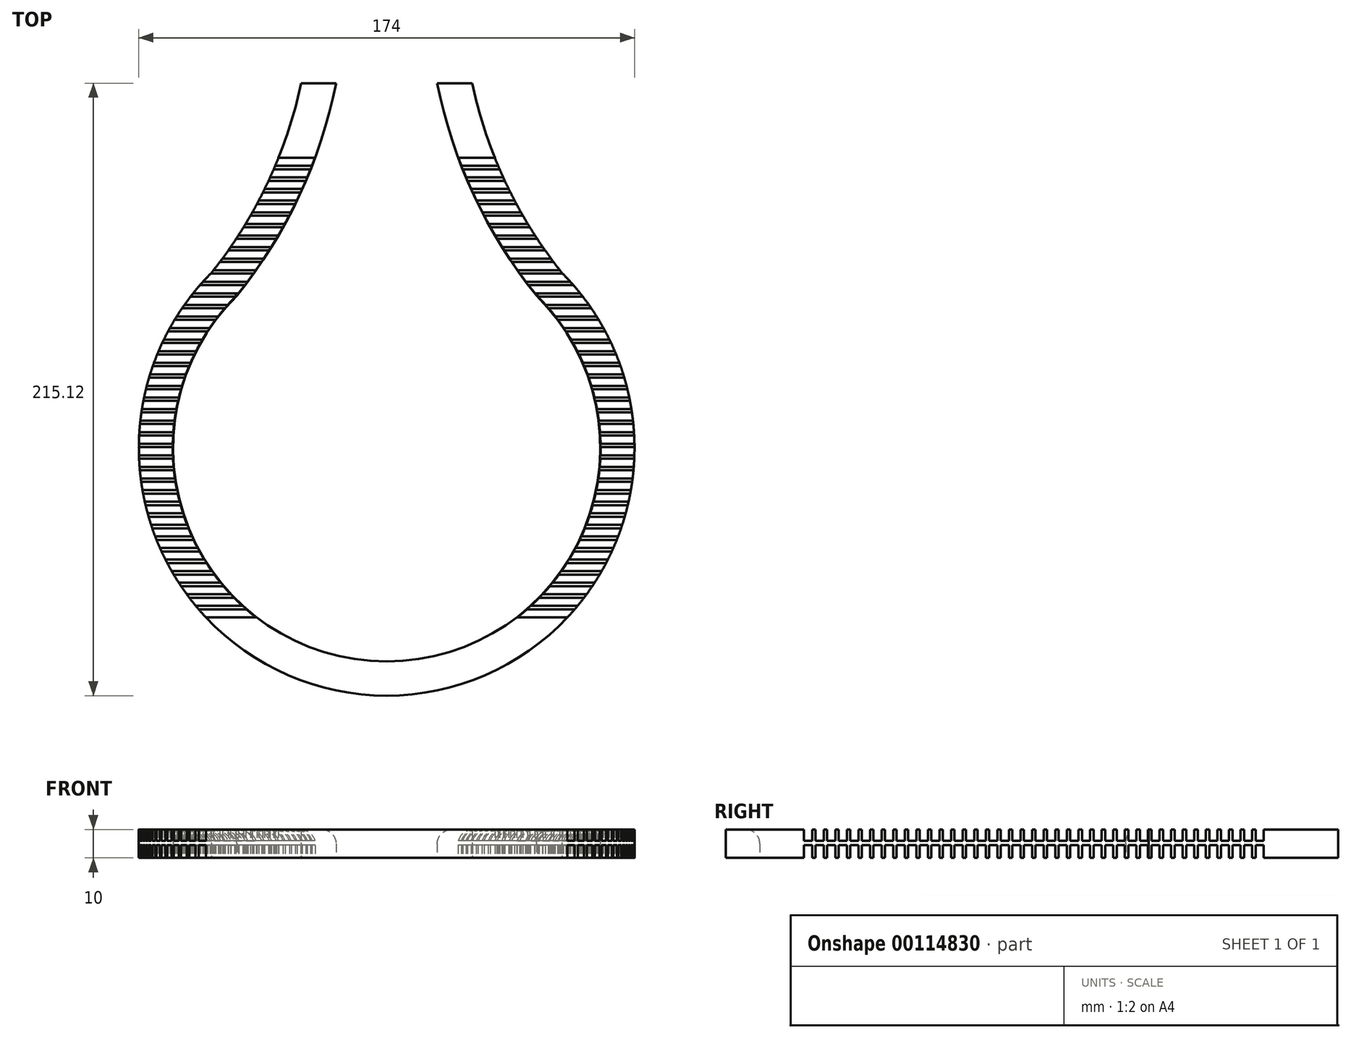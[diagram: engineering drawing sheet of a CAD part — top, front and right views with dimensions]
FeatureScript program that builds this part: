
annotation { "Feature Type Name" : "Feature", "Feature Type Description" : "" }
export const myFeature = defineFeature(function(context is Context, id is Id, definition is map)
    precondition{}
    {
        {
            var Q0;
            Q0=qCreatedBy(makeId("Top.planeOp"),FACE);
            var sketch = newSketch(context, id + "F0", { "sketchPlane" : qUnion([Q0])});
            skArc(sketch, "E0", {"start": v(-52.59, 53.48) * mm, "mid": v(0, -75) * mm, "end": v(52.59, 53.48) * mm});
            skArc(sketch, "E1.0", {"start": v(-61.52, 61.52) * mm, "mid": v(0, -87) * mm, "end": v(61.52, 61.52) * mm});
            skLineSegment(sketch, "E2.bottom", {"start": v(-30, 128.12) * mm, "end": v(-17.75, 128.12) * mm});
            skLineSegment(sketch, "E3", {"start": v(0, 0) * mm, "end": v(-86.34, 86.34) * mm, "construction": true});
            skLineSegment(sketch, "E4", {"start": v(0, 0) * mm, "end": v(95.2, 95.2) * mm, "construction": true});
            skArc(sketch, "E5", {"start": v(-61.52, 61.52) * mm, "mid": v(-41.87, 92.98) * mm, "end": v(-30, 128.12) * mm});
            skArc(sketch, "E6", {"start": v(30, 128.12) * mm, "mid": v(41.87, 92.98) * mm, "end": v(61.52, 61.52) * mm});
            skArc(sketch, "E7.0", {"start": v(-60.47, 44.37) * mm, "mid": v(-33.27, 83.27) * mm, "end": v(-17.75, 128.12) * mm});
            skArc(sketch, "E8.0", {"start": v(17.75, 128.12) * mm, "mid": v(33.27, 83.27) * mm, "end": v(60.47, 44.37) * mm});
            skLineSegment(sketch, "E9", {"start": v(17.75, 128.12) * mm, "end": v(30, 128.12) * mm});
            skSolve(sketch);
        }
        {
            var Q0;
            Q0=makeQuery(id+"F0.imprint","IMPRINT",FACE,{"disambiguationData":[TD([[makeQuery(id+"F0.imprint","IMPRINT",EDGE,{"derivedFrom":sQuery(id+"F0.wireOp",EDGE,"E1.0")}),1.0]])]});
            extrude(context, id + "F1", {"entities" : qUnion([Q0]), "depth" : 10 * mm});
        }
        {
            var Q0;
            Q0=makeQuery(id+"F1.opExtrude","CAP_EDGE",EDGE,{"disambiguationData":[OSD([sQuery(id+"F0.wireOp",EDGE,"C6nhFyBn-AcIP-nM1O-XMea-t3bKsUY3vbU9")])],"isStart":false});
            var Q1;
            Q1=makeQuery(id+"F1.opExtrude","CAP_EDGE",EDGE,{"disambiguationData":[OSD([sQuery(id+"F0.wireOp",EDGE,"zSkOm855-7VtX-evfV-GfkE-zdd4aLVwG0iK")])],"isStart":false});
            var Q2;
            Q2=makeQuery(id+"F1.opExtrude","CAP_EDGE",EDGE,{"disambiguationData":[OSD([sQuery(id+"F0.wireOp",EDGE,"E0")])],"isStart":false});
            var Q3;
            Q3=makeQuery(id+"F1.opExtrude","CAP_EDGE",EDGE,{"disambiguationData":[OSD([sQuery(id+"F0.wireOp",EDGE,"E7.0")])],"isStart":false});
            var Q4;
            Q4=makeQuery(id+"F1.opExtrude","CAP_EDGE",EDGE,{"disambiguationData":[OSD([sQuery(id+"F0.wireOp",EDGE,"E8.0")])],"isStart":false});
            fillet(context, id + "F2", {"entities" : qUnion([Q0, Q1, Q2, Q3, Q4]), "radius" : 5 * mm, "tangentPropagation" : true, "allowEdgeOverflow" : false});
        }
        {
            var Q0;
            Q0=qCreatedBy(makeId("Right.planeOp"),FACE);
            var sketch = newSketch(context, id + "F3", { "sketchPlane" : qUnion([Q0])});
            skLineSegment(sketch, "E10", {"start": v(109.77, 6) * mm, "end": v(-73.02, 6) * mm, "construction": true});
            skLineSegment(sketch, "E11", {"start": v(-73.72, 4.5) * mm, "end": v(109.9, 4.5) * mm, "construction": true});
            skLineSegment(sketch, "E12.bottom", {"start": v(101.9, 6) * mm, "end": v(99.07, 6) * mm});
            skLineSegment(sketch, "E12.top", {"start": v(101.9, 11.77) * mm, "end": v(99.07, 11.77) * mm});
            skLineSegment(sketch, "E12.left", {"start": v(101.9, 6) * mm, "end": v(101.9, 11.77) * mm});
            skLineSegment(sketch, "E12.right", {"start": v(99.07, 6) * mm, "end": v(99.07, 11.77) * mm});
            skLineSegment(sketch, "E13.0.1.0", {"start": v(101.9, -1.3) * mm, "end": v(101.9, 4.47) * mm});
            skLineSegment(sketch, "E13.0.1.1", {"start": v(101.9, 4.47) * mm, "end": v(99.07, 4.47) * mm});
            skLineSegment(sketch, "E13.0.1.2", {"start": v(99.07, -1.3) * mm, "end": v(99.07, 4.47) * mm});
            skLineSegment(sketch, "E13.0.1.3", {"start": v(101.9, -1.3) * mm, "end": v(99.07, -1.3) * mm});
            skLineSegment(sketch, "E13.1.0.0", {"start": v(97.83, 6) * mm, "end": v(97.83, 11.77) * mm});
            skLineSegment(sketch, "E13.1.0.1", {"start": v(97.83, 11.77) * mm, "end": v(95, 11.77) * mm});
            skLineSegment(sketch, "E13.1.0.2", {"start": v(95, 6) * mm, "end": v(95, 11.77) * mm});
            skLineSegment(sketch, "E13.1.0.3", {"start": v(97.83, 6) * mm, "end": v(95, 6) * mm});
            skLineSegment(sketch, "E13.1.1.0", {"start": v(97.83, -1.3) * mm, "end": v(97.83, 4.47) * mm});
            skLineSegment(sketch, "E13.1.1.1", {"start": v(97.83, 4.47) * mm, "end": v(95, 4.47) * mm});
            skLineSegment(sketch, "E13.1.1.2", {"start": v(95, -1.3) * mm, "end": v(95, 4.47) * mm});
            skLineSegment(sketch, "E13.1.1.3", {"start": v(97.83, -1.3) * mm, "end": v(95, -1.3) * mm});
            skLineSegment(sketch, "E13.2.0.0", {"start": v(93.76, 6) * mm, "end": v(93.76, 11.77) * mm});
            skLineSegment(sketch, "E13.2.0.1", {"start": v(93.76, 11.77) * mm, "end": v(90.94, 11.77) * mm});
            skLineSegment(sketch, "E13.2.0.2", {"start": v(90.94, 6) * mm, "end": v(90.94, 11.77) * mm});
            skLineSegment(sketch, "E13.2.0.3", {"start": v(93.76, 6) * mm, "end": v(90.94, 6) * mm});
            skLineSegment(sketch, "E13.2.1.0", {"start": v(93.76, -1.3) * mm, "end": v(93.76, 4.47) * mm});
            skLineSegment(sketch, "E13.2.1.1", {"start": v(93.76, 4.47) * mm, "end": v(90.94, 4.47) * mm});
            skLineSegment(sketch, "E13.2.1.2", {"start": v(90.94, -1.3) * mm, "end": v(90.94, 4.47) * mm});
            skLineSegment(sketch, "E13.2.1.3", {"start": v(93.76, -1.3) * mm, "end": v(90.94, -1.3) * mm});
            skLineSegment(sketch, "E13.3.0.0", {"start": v(89.7, 6) * mm, "end": v(89.7, 11.77) * mm});
            skLineSegment(sketch, "E13.3.0.1", {"start": v(89.7, 11.77) * mm, "end": v(86.87, 11.77) * mm});
            skLineSegment(sketch, "E13.3.0.2", {"start": v(86.87, 6) * mm, "end": v(86.87, 11.77) * mm});
            skLineSegment(sketch, "E13.3.0.3", {"start": v(89.7, 6) * mm, "end": v(86.87, 6) * mm});
            skLineSegment(sketch, "E13.3.1.0", {"start": v(89.7, -1.3) * mm, "end": v(89.7, 4.47) * mm});
            skLineSegment(sketch, "E13.3.1.1", {"start": v(89.7, 4.47) * mm, "end": v(86.87, 4.47) * mm});
            skLineSegment(sketch, "E13.3.1.2", {"start": v(86.87, -1.3) * mm, "end": v(86.87, 4.47) * mm});
            skLineSegment(sketch, "E13.3.1.3", {"start": v(89.7, -1.3) * mm, "end": v(86.87, -1.3) * mm});
            skLineSegment(sketch, "E13.4.0.0", {"start": v(85.63, 6) * mm, "end": v(85.63, 11.77) * mm});
            skLineSegment(sketch, "E13.4.0.1", {"start": v(85.63, 11.77) * mm, "end": v(82.8, 11.77) * mm});
            skLineSegment(sketch, "E13.4.0.2", {"start": v(82.8, 6) * mm, "end": v(82.8, 11.77) * mm});
            skLineSegment(sketch, "E13.4.0.3", {"start": v(85.63, 6) * mm, "end": v(82.8, 6) * mm});
            skLineSegment(sketch, "E13.4.1.0", {"start": v(85.63, -1.3) * mm, "end": v(85.63, 4.47) * mm});
            skLineSegment(sketch, "E13.4.1.1", {"start": v(85.63, 4.47) * mm, "end": v(82.8, 4.47) * mm});
            skLineSegment(sketch, "E13.4.1.2", {"start": v(82.8, -1.3) * mm, "end": v(82.8, 4.47) * mm});
            skLineSegment(sketch, "E13.4.1.3", {"start": v(85.63, -1.3) * mm, "end": v(82.8, -1.3) * mm});
            skLineSegment(sketch, "E13.5.0.0", {"start": v(81.57, 6) * mm, "end": v(81.57, 11.77) * mm});
            skLineSegment(sketch, "E13.5.0.1", {"start": v(81.57, 11.77) * mm, "end": v(78.74, 11.77) * mm});
            skLineSegment(sketch, "E13.5.0.2", {"start": v(78.74, 6) * mm, "end": v(78.74, 11.77) * mm});
            skLineSegment(sketch, "E13.5.0.3", {"start": v(81.57, 6) * mm, "end": v(78.74, 6) * mm});
            skLineSegment(sketch, "E13.5.1.0", {"start": v(81.57, -1.3) * mm, "end": v(81.57, 4.47) * mm});
            skLineSegment(sketch, "E13.5.1.1", {"start": v(81.57, 4.47) * mm, "end": v(78.74, 4.47) * mm});
            skLineSegment(sketch, "E13.5.1.2", {"start": v(78.74, -1.3) * mm, "end": v(78.74, 4.47) * mm});
            skLineSegment(sketch, "E13.5.1.3", {"start": v(81.57, -1.3) * mm, "end": v(78.74, -1.3) * mm});
            skLineSegment(sketch, "E13.6.0.0", {"start": v(77.5, 6) * mm, "end": v(77.5, 11.77) * mm});
            skLineSegment(sketch, "E13.6.0.1", {"start": v(77.5, 11.77) * mm, "end": v(74.67, 11.77) * mm});
            skLineSegment(sketch, "E13.6.0.2", {"start": v(74.67, 6) * mm, "end": v(74.67, 11.77) * mm});
            skLineSegment(sketch, "E13.6.0.3", {"start": v(77.5, 6) * mm, "end": v(74.67, 6) * mm});
            skLineSegment(sketch, "E13.6.1.0", {"start": v(77.5, -1.3) * mm, "end": v(77.5, 4.47) * mm});
            skLineSegment(sketch, "E13.6.1.1", {"start": v(77.5, 4.47) * mm, "end": v(74.67, 4.47) * mm});
            skLineSegment(sketch, "E13.6.1.2", {"start": v(74.67, -1.3) * mm, "end": v(74.67, 4.47) * mm});
            skLineSegment(sketch, "E13.6.1.3", {"start": v(77.5, -1.3) * mm, "end": v(74.67, -1.3) * mm});
            skLineSegment(sketch, "E13.7.0.0", {"start": v(73.44, 6) * mm, "end": v(73.44, 11.77) * mm});
            skLineSegment(sketch, "E13.7.0.1", {"start": v(73.44, 11.77) * mm, "end": v(70.6, 11.77) * mm});
            skLineSegment(sketch, "E13.7.0.2", {"start": v(70.6, 6) * mm, "end": v(70.6, 11.77) * mm});
            skLineSegment(sketch, "E13.7.0.3", {"start": v(73.44, 6) * mm, "end": v(70.6, 6) * mm});
            skLineSegment(sketch, "E13.7.1.0", {"start": v(73.44, -1.3) * mm, "end": v(73.44, 4.47) * mm});
            skLineSegment(sketch, "E13.7.1.1", {"start": v(73.44, 4.47) * mm, "end": v(70.6, 4.47) * mm});
            skLineSegment(sketch, "E13.7.1.2", {"start": v(70.6, -1.3) * mm, "end": v(70.6, 4.47) * mm});
            skLineSegment(sketch, "E13.7.1.3", {"start": v(73.44, -1.3) * mm, "end": v(70.6, -1.3) * mm});
            skLineSegment(sketch, "E13.8.0.0", {"start": v(69.37, 6) * mm, "end": v(69.37, 11.77) * mm});
            skLineSegment(sketch, "E13.8.0.1", {"start": v(69.37, 11.77) * mm, "end": v(66.54, 11.77) * mm});
            skLineSegment(sketch, "E13.8.0.2", {"start": v(66.54, 6) * mm, "end": v(66.54, 11.77) * mm});
            skLineSegment(sketch, "E13.8.0.3", {"start": v(69.37, 6) * mm, "end": v(66.54, 6) * mm});
            skLineSegment(sketch, "E13.8.1.0", {"start": v(69.37, -1.3) * mm, "end": v(69.37, 4.47) * mm});
            skLineSegment(sketch, "E13.8.1.1", {"start": v(69.37, 4.47) * mm, "end": v(66.54, 4.47) * mm});
            skLineSegment(sketch, "E13.8.1.2", {"start": v(66.54, -1.3) * mm, "end": v(66.54, 4.47) * mm});
            skLineSegment(sketch, "E13.8.1.3", {"start": v(69.37, -1.3) * mm, "end": v(66.54, -1.3) * mm});
            skLineSegment(sketch, "E13.9.0.0", {"start": v(65.3, 6) * mm, "end": v(65.3, 11.77) * mm});
            skLineSegment(sketch, "E13.9.0.1", {"start": v(65.3, 11.77) * mm, "end": v(62.48, 11.77) * mm});
            skLineSegment(sketch, "E13.9.0.2", {"start": v(62.48, 6) * mm, "end": v(62.48, 11.77) * mm});
            skLineSegment(sketch, "E13.9.0.3", {"start": v(65.3, 6) * mm, "end": v(62.48, 6) * mm});
            skLineSegment(sketch, "E13.9.1.0", {"start": v(65.3, -1.3) * mm, "end": v(65.3, 4.47) * mm});
            skLineSegment(sketch, "E13.9.1.1", {"start": v(65.3, 4.47) * mm, "end": v(62.48, 4.47) * mm});
            skLineSegment(sketch, "E13.9.1.2", {"start": v(62.48, -1.3) * mm, "end": v(62.48, 4.47) * mm});
            skLineSegment(sketch, "E13.9.1.3", {"start": v(65.3, -1.3) * mm, "end": v(62.48, -1.3) * mm});
            skLineSegment(sketch, "E13.10.0.0", {"start": v(61.24, 6) * mm, "end": v(61.24, 11.77) * mm});
            skLineSegment(sketch, "E13.10.0.1", {"start": v(61.24, 11.77) * mm, "end": v(58.41, 11.77) * mm});
            skLineSegment(sketch, "E13.10.0.2", {"start": v(58.41, 6) * mm, "end": v(58.41, 11.77) * mm});
            skLineSegment(sketch, "E13.10.0.3", {"start": v(61.24, 6) * mm, "end": v(58.41, 6) * mm});
            skLineSegment(sketch, "E13.10.1.0", {"start": v(61.24, -1.3) * mm, "end": v(61.24, 4.47) * mm});
            skLineSegment(sketch, "E13.10.1.1", {"start": v(61.24, 4.47) * mm, "end": v(58.41, 4.47) * mm});
            skLineSegment(sketch, "E13.10.1.2", {"start": v(58.41, -1.3) * mm, "end": v(58.41, 4.47) * mm});
            skLineSegment(sketch, "E13.10.1.3", {"start": v(61.24, -1.3) * mm, "end": v(58.41, -1.3) * mm});
            skLineSegment(sketch, "E13.11.0.0", {"start": v(57.17, 6) * mm, "end": v(57.17, 11.77) * mm});
            skLineSegment(sketch, "E13.11.0.1", {"start": v(57.17, 11.77) * mm, "end": v(54.35, 11.77) * mm});
            skLineSegment(sketch, "E13.11.0.2", {"start": v(54.35, 6) * mm, "end": v(54.35, 11.77) * mm});
            skLineSegment(sketch, "E13.11.0.3", {"start": v(57.17, 6) * mm, "end": v(54.35, 6) * mm});
            skLineSegment(sketch, "E13.11.1.0", {"start": v(57.17, -1.3) * mm, "end": v(57.17, 4.47) * mm});
            skLineSegment(sketch, "E13.11.1.1", {"start": v(57.17, 4.47) * mm, "end": v(54.35, 4.47) * mm});
            skLineSegment(sketch, "E13.11.1.2", {"start": v(54.35, -1.3) * mm, "end": v(54.35, 4.47) * mm});
            skLineSegment(sketch, "E13.11.1.3", {"start": v(57.17, -1.3) * mm, "end": v(54.35, -1.3) * mm});
            skLineSegment(sketch, "E13.12.0.0", {"start": v(53.1, 6) * mm, "end": v(53.1, 11.77) * mm});
            skLineSegment(sketch, "E13.12.0.1", {"start": v(53.1, 11.77) * mm, "end": v(50.28, 11.77) * mm});
            skLineSegment(sketch, "E13.12.0.2", {"start": v(50.28, 6) * mm, "end": v(50.28, 11.77) * mm});
            skLineSegment(sketch, "E13.12.0.3", {"start": v(53.1, 6) * mm, "end": v(50.28, 6) * mm});
            skLineSegment(sketch, "E13.12.1.0", {"start": v(53.1, -1.3) * mm, "end": v(53.1, 4.47) * mm});
            skLineSegment(sketch, "E13.12.1.1", {"start": v(53.1, 4.47) * mm, "end": v(50.28, 4.47) * mm});
            skLineSegment(sketch, "E13.12.1.2", {"start": v(50.28, -1.3) * mm, "end": v(50.28, 4.47) * mm});
            skLineSegment(sketch, "E13.12.1.3", {"start": v(53.1, -1.3) * mm, "end": v(50.28, -1.3) * mm});
            skLineSegment(sketch, "E13.13.0.0", {"start": v(49.04, 6) * mm, "end": v(49.04, 11.77) * mm});
            skLineSegment(sketch, "E13.13.0.1", {"start": v(49.04, 11.77) * mm, "end": v(46.22, 11.77) * mm});
            skLineSegment(sketch, "E13.13.0.2", {"start": v(46.22, 6) * mm, "end": v(46.22, 11.77) * mm});
            skLineSegment(sketch, "E13.13.0.3", {"start": v(49.04, 6) * mm, "end": v(46.22, 6) * mm});
            skLineSegment(sketch, "E13.13.1.0", {"start": v(49.04, -1.3) * mm, "end": v(49.04, 4.47) * mm});
            skLineSegment(sketch, "E13.13.1.1", {"start": v(49.04, 4.47) * mm, "end": v(46.22, 4.47) * mm});
            skLineSegment(sketch, "E13.13.1.2", {"start": v(46.22, -1.3) * mm, "end": v(46.22, 4.47) * mm});
            skLineSegment(sketch, "E13.13.1.3", {"start": v(49.04, -1.3) * mm, "end": v(46.22, -1.3) * mm});
            skLineSegment(sketch, "E13.14.0.0", {"start": v(44.98, 6) * mm, "end": v(44.98, 11.77) * mm});
            skLineSegment(sketch, "E13.14.0.1", {"start": v(44.98, 11.77) * mm, "end": v(42.15, 11.77) * mm});
            skLineSegment(sketch, "E13.14.0.2", {"start": v(42.15, 6) * mm, "end": v(42.15, 11.77) * mm});
            skLineSegment(sketch, "E13.14.0.3", {"start": v(44.98, 6) * mm, "end": v(42.15, 6) * mm});
            skLineSegment(sketch, "E13.14.1.0", {"start": v(44.98, -1.3) * mm, "end": v(44.98, 4.47) * mm});
            skLineSegment(sketch, "E13.14.1.1", {"start": v(44.98, 4.47) * mm, "end": v(42.15, 4.47) * mm});
            skLineSegment(sketch, "E13.14.1.2", {"start": v(42.15, -1.3) * mm, "end": v(42.15, 4.47) * mm});
            skLineSegment(sketch, "E13.14.1.3", {"start": v(44.98, -1.3) * mm, "end": v(42.15, -1.3) * mm});
            skLineSegment(sketch, "E13.15.0.0", {"start": v(40.91, 6) * mm, "end": v(40.91, 11.77) * mm});
            skLineSegment(sketch, "E13.15.0.1", {"start": v(40.91, 11.77) * mm, "end": v(38.09, 11.77) * mm});
            skLineSegment(sketch, "E13.15.0.2", {"start": v(38.09, 6) * mm, "end": v(38.09, 11.77) * mm});
            skLineSegment(sketch, "E13.15.0.3", {"start": v(40.91, 6) * mm, "end": v(38.09, 6) * mm});
            skLineSegment(sketch, "E13.15.1.0", {"start": v(40.91, -1.3) * mm, "end": v(40.91, 4.47) * mm});
            skLineSegment(sketch, "E13.15.1.1", {"start": v(40.91, 4.47) * mm, "end": v(38.09, 4.47) * mm});
            skLineSegment(sketch, "E13.15.1.2", {"start": v(38.09, -1.3) * mm, "end": v(38.09, 4.47) * mm});
            skLineSegment(sketch, "E13.15.1.3", {"start": v(40.91, -1.3) * mm, "end": v(38.09, -1.3) * mm});
            skLineSegment(sketch, "E13.16.0.0", {"start": v(36.85, 6) * mm, "end": v(36.85, 11.77) * mm});
            skLineSegment(sketch, "E13.16.0.1", {"start": v(36.85, 11.77) * mm, "end": v(34.02, 11.77) * mm});
            skLineSegment(sketch, "E13.16.0.2", {"start": v(34.02, 6) * mm, "end": v(34.02, 11.77) * mm});
            skLineSegment(sketch, "E13.16.0.3", {"start": v(36.85, 6) * mm, "end": v(34.02, 6) * mm});
            skLineSegment(sketch, "E13.16.1.0", {"start": v(36.85, -1.3) * mm, "end": v(36.85, 4.47) * mm});
            skLineSegment(sketch, "E13.16.1.1", {"start": v(36.85, 4.47) * mm, "end": v(34.02, 4.47) * mm});
            skLineSegment(sketch, "E13.16.1.2", {"start": v(34.02, -1.3) * mm, "end": v(34.02, 4.47) * mm});
            skLineSegment(sketch, "E13.16.1.3", {"start": v(36.85, -1.3) * mm, "end": v(34.02, -1.3) * mm});
            skLineSegment(sketch, "E13.17.0.0", {"start": v(32.78, 6) * mm, "end": v(32.78, 11.77) * mm});
            skLineSegment(sketch, "E13.17.0.1", {"start": v(32.78, 11.77) * mm, "end": v(29.96, 11.77) * mm});
            skLineSegment(sketch, "E13.17.0.2", {"start": v(29.96, 6) * mm, "end": v(29.96, 11.77) * mm});
            skLineSegment(sketch, "E13.17.0.3", {"start": v(32.78, 6) * mm, "end": v(29.96, 6) * mm});
            skLineSegment(sketch, "E13.17.1.0", {"start": v(32.78, -1.3) * mm, "end": v(32.78, 4.47) * mm});
            skLineSegment(sketch, "E13.17.1.1", {"start": v(32.78, 4.47) * mm, "end": v(29.96, 4.47) * mm});
            skLineSegment(sketch, "E13.17.1.2", {"start": v(29.96, -1.3) * mm, "end": v(29.96, 4.47) * mm});
            skLineSegment(sketch, "E13.17.1.3", {"start": v(32.78, -1.3) * mm, "end": v(29.96, -1.3) * mm});
            skLineSegment(sketch, "E13.18.0.0", {"start": v(28.72, 6) * mm, "end": v(28.72, 11.77) * mm});
            skLineSegment(sketch, "E13.18.0.1", {"start": v(28.72, 11.77) * mm, "end": v(25.9, 11.77) * mm});
            skLineSegment(sketch, "E13.18.0.2", {"start": v(25.9, 6) * mm, "end": v(25.9, 11.77) * mm});
            skLineSegment(sketch, "E13.18.0.3", {"start": v(28.72, 6) * mm, "end": v(25.9, 6) * mm});
            skLineSegment(sketch, "E13.18.1.0", {"start": v(28.72, -1.3) * mm, "end": v(28.72, 4.47) * mm});
            skLineSegment(sketch, "E13.18.1.1", {"start": v(28.72, 4.47) * mm, "end": v(25.9, 4.47) * mm});
            skLineSegment(sketch, "E13.18.1.2", {"start": v(25.9, -1.3) * mm, "end": v(25.9, 4.47) * mm});
            skLineSegment(sketch, "E13.18.1.3", {"start": v(28.72, -1.3) * mm, "end": v(25.9, -1.3) * mm});
            skLineSegment(sketch, "E13.19.0.0", {"start": v(24.65, 6) * mm, "end": v(24.65, 11.77) * mm});
            skLineSegment(sketch, "E13.19.0.1", {"start": v(24.65, 11.77) * mm, "end": v(21.83, 11.77) * mm});
            skLineSegment(sketch, "E13.19.0.2", {"start": v(21.83, 6) * mm, "end": v(21.83, 11.77) * mm});
            skLineSegment(sketch, "E13.19.0.3", {"start": v(24.65, 6) * mm, "end": v(21.83, 6) * mm});
            skLineSegment(sketch, "E13.19.1.0", {"start": v(24.65, -1.3) * mm, "end": v(24.65, 4.47) * mm});
            skLineSegment(sketch, "E13.19.1.1", {"start": v(24.65, 4.47) * mm, "end": v(21.83, 4.47) * mm});
            skLineSegment(sketch, "E13.19.1.2", {"start": v(21.83, -1.3) * mm, "end": v(21.83, 4.47) * mm});
            skLineSegment(sketch, "E13.19.1.3", {"start": v(24.65, -1.3) * mm, "end": v(21.83, -1.3) * mm});
            skLineSegment(sketch, "E13.20.0.0", {"start": v(20.59, 6) * mm, "end": v(20.59, 11.77) * mm});
            skLineSegment(sketch, "E13.20.0.1", {"start": v(20.59, 11.77) * mm, "end": v(17.76, 11.77) * mm});
            skLineSegment(sketch, "E13.20.0.2", {"start": v(17.76, 6) * mm, "end": v(17.76, 11.77) * mm});
            skLineSegment(sketch, "E13.20.0.3", {"start": v(20.59, 6) * mm, "end": v(17.76, 6) * mm});
            skLineSegment(sketch, "E13.20.1.0", {"start": v(20.59, -1.3) * mm, "end": v(20.59, 4.47) * mm});
            skLineSegment(sketch, "E13.20.1.1", {"start": v(20.59, 4.47) * mm, "end": v(17.76, 4.47) * mm});
            skLineSegment(sketch, "E13.20.1.2", {"start": v(17.76, -1.3) * mm, "end": v(17.76, 4.47) * mm});
            skLineSegment(sketch, "E13.20.1.3", {"start": v(20.59, -1.3) * mm, "end": v(17.76, -1.3) * mm});
            skLineSegment(sketch, "E13.21.0.0", {"start": v(16.52, 6) * mm, "end": v(16.52, 11.77) * mm});
            skLineSegment(sketch, "E13.21.0.1", {"start": v(16.52, 11.77) * mm, "end": v(13.7, 11.77) * mm});
            skLineSegment(sketch, "E13.21.0.2", {"start": v(13.7, 6) * mm, "end": v(13.7, 11.77) * mm});
            skLineSegment(sketch, "E13.21.0.3", {"start": v(16.52, 6) * mm, "end": v(13.7, 6) * mm});
            skLineSegment(sketch, "E13.21.1.0", {"start": v(16.52, -1.3) * mm, "end": v(16.52, 4.47) * mm});
            skLineSegment(sketch, "E13.21.1.1", {"start": v(16.52, 4.47) * mm, "end": v(13.7, 4.47) * mm});
            skLineSegment(sketch, "E13.21.1.2", {"start": v(13.7, -1.3) * mm, "end": v(13.7, 4.47) * mm});
            skLineSegment(sketch, "E13.21.1.3", {"start": v(16.52, -1.3) * mm, "end": v(13.7, -1.3) * mm});
            skLineSegment(sketch, "E13.22.0.0", {"start": v(12.46, 6) * mm, "end": v(12.46, 11.77) * mm});
            skLineSegment(sketch, "E13.22.0.1", {"start": v(12.46, 11.77) * mm, "end": v(9.63, 11.77) * mm});
            skLineSegment(sketch, "E13.22.0.2", {"start": v(9.63, 6) * mm, "end": v(9.63, 11.77) * mm});
            skLineSegment(sketch, "E13.22.0.3", {"start": v(12.46, 6) * mm, "end": v(9.63, 6) * mm});
            skLineSegment(sketch, "E13.22.1.0", {"start": v(12.46, -1.3) * mm, "end": v(12.46, 4.47) * mm});
            skLineSegment(sketch, "E13.22.1.1", {"start": v(12.46, 4.47) * mm, "end": v(9.63, 4.47) * mm});
            skLineSegment(sketch, "E13.22.1.2", {"start": v(9.63, -1.3) * mm, "end": v(9.63, 4.47) * mm});
            skLineSegment(sketch, "E13.22.1.3", {"start": v(12.46, -1.3) * mm, "end": v(9.63, -1.3) * mm});
            skLineSegment(sketch, "E13.23.0.0", {"start": v(8.4, 6) * mm, "end": v(8.4, 11.77) * mm});
            skLineSegment(sketch, "E13.23.0.1", {"start": v(8.4, 11.77) * mm, "end": v(5.56, 11.77) * mm});
            skLineSegment(sketch, "E13.23.0.2", {"start": v(5.56, 6) * mm, "end": v(5.56, 11.77) * mm});
            skLineSegment(sketch, "E13.23.0.3", {"start": v(8.4, 6) * mm, "end": v(5.56, 6) * mm});
            skLineSegment(sketch, "E13.23.1.0", {"start": v(8.4, -1.3) * mm, "end": v(8.4, 4.47) * mm});
            skLineSegment(sketch, "E13.23.1.1", {"start": v(8.4, 4.47) * mm, "end": v(5.56, 4.47) * mm});
            skLineSegment(sketch, "E13.23.1.2", {"start": v(5.56, -1.3) * mm, "end": v(5.56, 4.47) * mm});
            skLineSegment(sketch, "E13.23.1.3", {"start": v(8.4, -1.3) * mm, "end": v(5.56, -1.3) * mm});
            skLineSegment(sketch, "E13.24.0.0", {"start": v(4.32, 6) * mm, "end": v(4.32, 11.77) * mm});
            skLineSegment(sketch, "E13.24.0.1", {"start": v(4.32, 11.77) * mm, "end": v(1.5, 11.77) * mm});
            skLineSegment(sketch, "E13.24.0.2", {"start": v(1.5, 6) * mm, "end": v(1.5, 11.77) * mm});
            skLineSegment(sketch, "E13.24.0.3", {"start": v(4.32, 6) * mm, "end": v(1.5, 6) * mm});
            skLineSegment(sketch, "E13.24.1.0", {"start": v(4.32, -1.3) * mm, "end": v(4.32, 4.47) * mm});
            skLineSegment(sketch, "E13.24.1.1", {"start": v(4.32, 4.47) * mm, "end": v(1.5, 4.47) * mm});
            skLineSegment(sketch, "E13.24.1.2", {"start": v(1.5, -1.3) * mm, "end": v(1.5, 4.47) * mm});
            skLineSegment(sketch, "E13.24.1.3", {"start": v(4.32, -1.3) * mm, "end": v(1.5, -1.3) * mm});
            skLineSegment(sketch, "E13.direction1", {"start": v(99.07, 6) * mm, "end": v(95, 6) * mm, "construction": true});
            skLineSegment(sketch, "E13.direction2", {"start": v(99.07, 6) * mm, "end": v(99.07, -1.3) * mm, "construction": true});
            skLineSegment(sketch, "E14.0.25.0", {"start": v(0.26, 6) * mm, "end": v(0.26, 11.77) * mm});
            skLineSegment(sketch, "E14.3.25.0", {"start": v(0.26, 11.77) * mm, "end": v(-2.57, 11.77) * mm});
            skLineSegment(sketch, "E14.6.25.0", {"start": v(-2.57, 6) * mm, "end": v(-2.57, 11.77) * mm});
            skLineSegment(sketch, "E14.9.25.0", {"start": v(0.26, 6) * mm, "end": v(-2.57, 6) * mm});
            skLineSegment(sketch, "E14.0.25.1", {"start": v(0.26, -1.3) * mm, "end": v(0.26, 4.47) * mm});
            skLineSegment(sketch, "E14.3.25.1", {"start": v(0.26, 4.47) * mm, "end": v(-2.57, 4.47) * mm});
            skLineSegment(sketch, "E14.6.25.1", {"start": v(-2.57, -1.3) * mm, "end": v(-2.57, 4.47) * mm});
            skLineSegment(sketch, "E14.9.25.1", {"start": v(0.26, -1.3) * mm, "end": v(-2.57, -1.3) * mm});
            skLineSegment(sketch, "E14.0.26.0", {"start": v(-3.8, 6) * mm, "end": v(-3.8, 11.77) * mm});
            skLineSegment(sketch, "E14.3.26.0", {"start": v(-3.8, 11.77) * mm, "end": v(-6.63, 11.77) * mm});
            skLineSegment(sketch, "E14.6.26.0", {"start": v(-6.63, 6) * mm, "end": v(-6.63, 11.77) * mm});
            skLineSegment(sketch, "E14.9.26.0", {"start": v(-3.8, 6) * mm, "end": v(-6.63, 6) * mm});
            skLineSegment(sketch, "E14.0.26.1", {"start": v(-3.8, -1.3) * mm, "end": v(-3.8, 4.47) * mm});
            skLineSegment(sketch, "E14.3.26.1", {"start": v(-3.8, 4.47) * mm, "end": v(-6.63, 4.47) * mm});
            skLineSegment(sketch, "E14.6.26.1", {"start": v(-6.63, -1.3) * mm, "end": v(-6.63, 4.47) * mm});
            skLineSegment(sketch, "E14.9.26.1", {"start": v(-3.8, -1.3) * mm, "end": v(-6.63, -1.3) * mm});
            skLineSegment(sketch, "E14.0.27.0", {"start": v(-7.87, 6) * mm, "end": v(-7.87, 11.77) * mm});
            skLineSegment(sketch, "E14.3.27.0", {"start": v(-7.87, 11.77) * mm, "end": v(-10.7, 11.77) * mm});
            skLineSegment(sketch, "E14.6.27.0", {"start": v(-10.7, 6) * mm, "end": v(-10.7, 11.77) * mm});
            skLineSegment(sketch, "E14.9.27.0", {"start": v(-7.87, 6) * mm, "end": v(-10.7, 6) * mm});
            skLineSegment(sketch, "E14.0.27.1", {"start": v(-7.87, -1.3) * mm, "end": v(-7.87, 4.47) * mm});
            skLineSegment(sketch, "E14.3.27.1", {"start": v(-7.87, 4.47) * mm, "end": v(-10.7, 4.47) * mm});
            skLineSegment(sketch, "E14.6.27.1", {"start": v(-10.7, -1.3) * mm, "end": v(-10.7, 4.47) * mm});
            skLineSegment(sketch, "E14.9.27.1", {"start": v(-7.87, -1.3) * mm, "end": v(-10.7, -1.3) * mm});
            skLineSegment(sketch, "E14.0.28.0", {"start": v(-11.94, 6) * mm, "end": v(-11.94, 11.77) * mm});
            skLineSegment(sketch, "E14.3.28.0", {"start": v(-11.94, 11.77) * mm, "end": v(-14.76, 11.77) * mm});
            skLineSegment(sketch, "E14.6.28.0", {"start": v(-14.76, 6) * mm, "end": v(-14.76, 11.77) * mm});
            skLineSegment(sketch, "E14.9.28.0", {"start": v(-11.94, 6) * mm, "end": v(-14.76, 6) * mm});
            skLineSegment(sketch, "E14.0.28.1", {"start": v(-11.94, -1.3) * mm, "end": v(-11.94, 4.47) * mm});
            skLineSegment(sketch, "E14.3.28.1", {"start": v(-11.94, 4.47) * mm, "end": v(-14.76, 4.47) * mm});
            skLineSegment(sketch, "E14.6.28.1", {"start": v(-14.76, -1.3) * mm, "end": v(-14.76, 4.47) * mm});
            skLineSegment(sketch, "E14.9.28.1", {"start": v(-11.94, -1.3) * mm, "end": v(-14.76, -1.3) * mm});
            skLineSegment(sketch, "E14.0.29.0", {"start": v(-16, 6) * mm, "end": v(-16, 11.77) * mm});
            skLineSegment(sketch, "E14.3.29.0", {"start": v(-16, 11.77) * mm, "end": v(-18.83, 11.77) * mm});
            skLineSegment(sketch, "E14.6.29.0", {"start": v(-18.83, 6) * mm, "end": v(-18.83, 11.77) * mm});
            skLineSegment(sketch, "E14.9.29.0", {"start": v(-16, 6) * mm, "end": v(-18.83, 6) * mm});
            skLineSegment(sketch, "E14.0.29.1", {"start": v(-16, -1.3) * mm, "end": v(-16, 4.47) * mm});
            skLineSegment(sketch, "E14.3.29.1", {"start": v(-16, 4.47) * mm, "end": v(-18.83, 4.47) * mm});
            skLineSegment(sketch, "E14.6.29.1", {"start": v(-18.83, -1.3) * mm, "end": v(-18.83, 4.47) * mm});
            skLineSegment(sketch, "E14.9.29.1", {"start": v(-16, -1.3) * mm, "end": v(-18.83, -1.3) * mm});
            skLineSegment(sketch, "E15.0.30.0", {"start": v(-20.07, 6) * mm, "end": v(-20.07, 11.77) * mm});
            skLineSegment(sketch, "E15.3.30.0", {"start": v(-20.07, 11.77) * mm, "end": v(-22.9, 11.77) * mm});
            skLineSegment(sketch, "E15.6.30.0", {"start": v(-22.9, 6) * mm, "end": v(-22.9, 11.77) * mm});
            skLineSegment(sketch, "E15.9.30.0", {"start": v(-20.07, 6) * mm, "end": v(-22.9, 6) * mm});
            skLineSegment(sketch, "E15.0.30.1", {"start": v(-20.07, -1.3) * mm, "end": v(-20.07, 4.47) * mm});
            skLineSegment(sketch, "E15.3.30.1", {"start": v(-20.07, 4.47) * mm, "end": v(-22.9, 4.47) * mm});
            skLineSegment(sketch, "E15.6.30.1", {"start": v(-22.9, -1.3) * mm, "end": v(-22.9, 4.47) * mm});
            skLineSegment(sketch, "E15.9.30.1", {"start": v(-20.07, -1.3) * mm, "end": v(-22.9, -1.3) * mm});
            skLineSegment(sketch, "E15.0.31.0", {"start": v(-24.13, 6) * mm, "end": v(-24.13, 11.77) * mm});
            skLineSegment(sketch, "E15.3.31.0", {"start": v(-24.13, 11.77) * mm, "end": v(-26.96, 11.77) * mm});
            skLineSegment(sketch, "E15.6.31.0", {"start": v(-26.96, 6) * mm, "end": v(-26.96, 11.77) * mm});
            skLineSegment(sketch, "E15.9.31.0", {"start": v(-24.13, 6) * mm, "end": v(-26.96, 6) * mm});
            skLineSegment(sketch, "E15.0.31.1", {"start": v(-24.13, -1.3) * mm, "end": v(-24.13, 4.47) * mm});
            skLineSegment(sketch, "E15.3.31.1", {"start": v(-24.13, 4.47) * mm, "end": v(-26.96, 4.47) * mm});
            skLineSegment(sketch, "E15.6.31.1", {"start": v(-26.96, -1.3) * mm, "end": v(-26.96, 4.47) * mm});
            skLineSegment(sketch, "E15.9.31.1", {"start": v(-24.13, -1.3) * mm, "end": v(-26.96, -1.3) * mm});
            skLineSegment(sketch, "E15.0.32.0", {"start": v(-28.2, 6) * mm, "end": v(-28.2, 11.77) * mm});
            skLineSegment(sketch, "E15.3.32.0", {"start": v(-28.2, 11.77) * mm, "end": v(-31.02, 11.77) * mm});
            skLineSegment(sketch, "E15.6.32.0", {"start": v(-31.02, 6) * mm, "end": v(-31.02, 11.77) * mm});
            skLineSegment(sketch, "E15.9.32.0", {"start": v(-28.2, 6) * mm, "end": v(-31.02, 6) * mm});
            skLineSegment(sketch, "E15.0.32.1", {"start": v(-28.2, -1.3) * mm, "end": v(-28.2, 4.47) * mm});
            skLineSegment(sketch, "E15.3.32.1", {"start": v(-28.2, 4.47) * mm, "end": v(-31.02, 4.47) * mm});
            skLineSegment(sketch, "E15.6.32.1", {"start": v(-31.02, -1.3) * mm, "end": v(-31.02, 4.47) * mm});
            skLineSegment(sketch, "E15.9.32.1", {"start": v(-28.2, -1.3) * mm, "end": v(-31.02, -1.3) * mm});
            skLineSegment(sketch, "E15.0.33.0", {"start": v(-32.26, 6) * mm, "end": v(-32.26, 11.77) * mm});
            skLineSegment(sketch, "E15.3.33.0", {"start": v(-32.26, 11.77) * mm, "end": v(-35.09, 11.77) * mm});
            skLineSegment(sketch, "E15.6.33.0", {"start": v(-35.09, 6) * mm, "end": v(-35.09, 11.77) * mm});
            skLineSegment(sketch, "E15.9.33.0", {"start": v(-32.26, 6) * mm, "end": v(-35.09, 6) * mm});
            skLineSegment(sketch, "E15.0.33.1", {"start": v(-32.26, -1.3) * mm, "end": v(-32.26, 4.47) * mm});
            skLineSegment(sketch, "E15.3.33.1", {"start": v(-32.26, 4.47) * mm, "end": v(-35.09, 4.47) * mm});
            skLineSegment(sketch, "E15.6.33.1", {"start": v(-35.09, -1.3) * mm, "end": v(-35.09, 4.47) * mm});
            skLineSegment(sketch, "E15.9.33.1", {"start": v(-32.26, -1.3) * mm, "end": v(-35.09, -1.3) * mm});
            skLineSegment(sketch, "E15.0.34.0", {"start": v(-36.33, 6) * mm, "end": v(-36.33, 11.77) * mm});
            skLineSegment(sketch, "E15.3.34.0", {"start": v(-36.33, 11.77) * mm, "end": v(-39.15, 11.77) * mm});
            skLineSegment(sketch, "E15.6.34.0", {"start": v(-39.15, 6) * mm, "end": v(-39.15, 11.77) * mm});
            skLineSegment(sketch, "E15.9.34.0", {"start": v(-36.33, 6) * mm, "end": v(-39.15, 6) * mm});
            skLineSegment(sketch, "E15.0.34.1", {"start": v(-36.33, -1.3) * mm, "end": v(-36.33, 4.47) * mm});
            skLineSegment(sketch, "E15.3.34.1", {"start": v(-36.33, 4.47) * mm, "end": v(-39.15, 4.47) * mm});
            skLineSegment(sketch, "E15.6.34.1", {"start": v(-39.15, -1.3) * mm, "end": v(-39.15, 4.47) * mm});
            skLineSegment(sketch, "E15.9.34.1", {"start": v(-36.33, -1.3) * mm, "end": v(-39.15, -1.3) * mm});
            skLineSegment(sketch, "E15.0.35.0", {"start": v(-40.4, 6) * mm, "end": v(-40.4, 11.77) * mm});
            skLineSegment(sketch, "E15.3.35.0", {"start": v(-40.4, 11.77) * mm, "end": v(-43.22, 11.77) * mm});
            skLineSegment(sketch, "E15.6.35.0", {"start": v(-43.22, 6) * mm, "end": v(-43.22, 11.77) * mm});
            skLineSegment(sketch, "E15.9.35.0", {"start": v(-40.4, 6) * mm, "end": v(-43.22, 6) * mm});
            skLineSegment(sketch, "E15.0.35.1", {"start": v(-40.4, -1.3) * mm, "end": v(-40.4, 4.47) * mm});
            skLineSegment(sketch, "E15.3.35.1", {"start": v(-40.4, 4.47) * mm, "end": v(-43.22, 4.47) * mm});
            skLineSegment(sketch, "E15.6.35.1", {"start": v(-43.22, -1.3) * mm, "end": v(-43.22, 4.47) * mm});
            skLineSegment(sketch, "E15.9.35.1", {"start": v(-40.4, -1.3) * mm, "end": v(-43.22, -1.3) * mm});
            skLineSegment(sketch, "E15.0.36.0", {"start": v(-44.46, 6) * mm, "end": v(-44.46, 11.77) * mm});
            skLineSegment(sketch, "E15.3.36.0", {"start": v(-44.46, 11.77) * mm, "end": v(-47.29, 11.77) * mm});
            skLineSegment(sketch, "E15.6.36.0", {"start": v(-47.29, 6) * mm, "end": v(-47.29, 11.77) * mm});
            skLineSegment(sketch, "E15.9.36.0", {"start": v(-44.46, 6) * mm, "end": v(-47.29, 6) * mm});
            skLineSegment(sketch, "E15.0.36.1", {"start": v(-44.46, -1.3) * mm, "end": v(-44.46, 4.47) * mm});
            skLineSegment(sketch, "E15.3.36.1", {"start": v(-44.46, 4.47) * mm, "end": v(-47.29, 4.47) * mm});
            skLineSegment(sketch, "E15.6.36.1", {"start": v(-47.29, -1.3) * mm, "end": v(-47.29, 4.47) * mm});
            skLineSegment(sketch, "E15.9.36.1", {"start": v(-44.46, -1.3) * mm, "end": v(-47.29, -1.3) * mm});
            skLineSegment(sketch, "E15.0.37.0", {"start": v(-48.52, 6) * mm, "end": v(-48.52, 11.77) * mm});
            skLineSegment(sketch, "E15.3.37.0", {"start": v(-48.52, 11.77) * mm, "end": v(-51.35, 11.77) * mm});
            skLineSegment(sketch, "E15.6.37.0", {"start": v(-51.35, 6) * mm, "end": v(-51.35, 11.77) * mm});
            skLineSegment(sketch, "E15.9.37.0", {"start": v(-48.52, 6) * mm, "end": v(-51.35, 6) * mm});
            skLineSegment(sketch, "E15.0.37.1", {"start": v(-48.52, -1.3) * mm, "end": v(-48.52, 4.47) * mm});
            skLineSegment(sketch, "E15.3.37.1", {"start": v(-48.52, 4.47) * mm, "end": v(-51.35, 4.47) * mm});
            skLineSegment(sketch, "E15.6.37.1", {"start": v(-51.35, -1.3) * mm, "end": v(-51.35, 4.47) * mm});
            skLineSegment(sketch, "E15.9.37.1", {"start": v(-48.52, -1.3) * mm, "end": v(-51.35, -1.3) * mm});
            skLineSegment(sketch, "E15.0.38.0", {"start": v(-52.59, 6) * mm, "end": v(-52.59, 11.77) * mm});
            skLineSegment(sketch, "E15.3.38.0", {"start": v(-52.59, 11.77) * mm, "end": v(-55.42, 11.77) * mm});
            skLineSegment(sketch, "E15.6.38.0", {"start": v(-55.42, 6) * mm, "end": v(-55.42, 11.77) * mm});
            skLineSegment(sketch, "E15.9.38.0", {"start": v(-52.59, 6) * mm, "end": v(-55.42, 6) * mm});
            skLineSegment(sketch, "E15.0.38.1", {"start": v(-52.59, -1.3) * mm, "end": v(-52.59, 4.47) * mm});
            skLineSegment(sketch, "E15.3.38.1", {"start": v(-52.59, 4.47) * mm, "end": v(-55.42, 4.47) * mm});
            skLineSegment(sketch, "E15.6.38.1", {"start": v(-55.42, -1.3) * mm, "end": v(-55.42, 4.47) * mm});
            skLineSegment(sketch, "E15.9.38.1", {"start": v(-52.59, -1.3) * mm, "end": v(-55.42, -1.3) * mm});
            skLineSegment(sketch, "E15.0.39.0", {"start": v(-56.65, 6) * mm, "end": v(-56.65, 11.77) * mm});
            skLineSegment(sketch, "E15.3.39.0", {"start": v(-56.65, 11.77) * mm, "end": v(-59.48, 11.77) * mm});
            skLineSegment(sketch, "E15.6.39.0", {"start": v(-59.48, 6) * mm, "end": v(-59.48, 11.77) * mm});
            skLineSegment(sketch, "E15.9.39.0", {"start": v(-56.65, 6) * mm, "end": v(-59.48, 6) * mm});
            skLineSegment(sketch, "E15.0.39.1", {"start": v(-56.65, -1.3) * mm, "end": v(-56.65, 4.47) * mm});
            skLineSegment(sketch, "E15.3.39.1", {"start": v(-56.65, 4.47) * mm, "end": v(-59.48, 4.47) * mm});
            skLineSegment(sketch, "E15.6.39.1", {"start": v(-59.48, -1.3) * mm, "end": v(-59.48, 4.47) * mm});
            skLineSegment(sketch, "E15.9.39.1", {"start": v(-56.65, -1.3) * mm, "end": v(-59.48, -1.3) * mm});
            skSolve(sketch);
        }
        {
            var Q0;
            Q0 = qSketchRegion(id + "F3", true);
            extrude(context, id + "F4", {"entities" : qUnion([Q0]), "operationType" : NewBodyOperationType.REMOVE, "endBound" : BoundingType.THROUGH_ALL, "depth" : 25 * mm, "hasSecondDirection" : true, "secondDirectionBound" : SecondDirectionBoundingType.THROUGH_ALL, "secondDirectionOppositeDirection" : true, "secondDirectionDepth" : 25 * mm});
        }
    });
